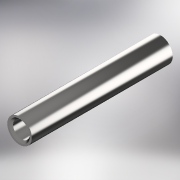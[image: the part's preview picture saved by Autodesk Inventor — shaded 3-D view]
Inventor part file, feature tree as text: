
AUTODESK INVENTOR PART (.ipt)
format: ipt  version: 2018.2 (Build 222227000, 227)  size: 118,784 bytes
history: native  units: mm
features: extrude x1, chamfer x1, sketch x1
ambient origin geometry x8: Origin, YZ Plane, XZ Plane, XY Plane, X Axis, Y Axis, Z Axis, Center Point
bodies: Solid1 (feature_tree)
feature tree (3):
  extrude  "Extrusion1"  Depth=55.0mm
  chamfer  "Chamfer1"  Distance=55.0mm
  sketch  "Sketch1"  dims[d0=6.55mm d1=9.6mm d2=55.0mm d3=0.0mm d4=0.75mm d5=2.0mm d6=45.0deg]
